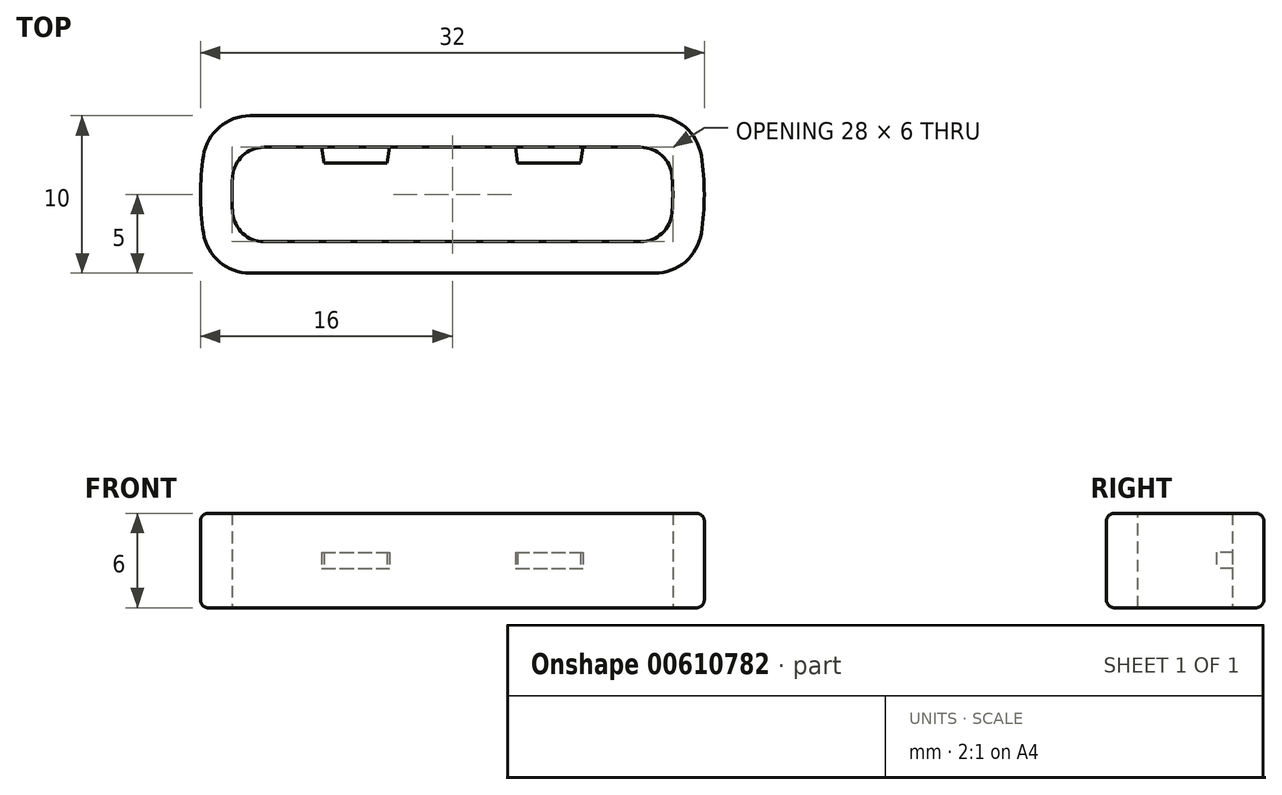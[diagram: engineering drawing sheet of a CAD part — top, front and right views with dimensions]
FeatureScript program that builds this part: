
annotation { "Feature Type Name" : "Feature", "Feature Type Description" : "" }
export const myFeature = defineFeature(function(context is Context, id is Id, definition is map)
    precondition{}
    {
        {
            var Q0;
            Q0=qCreatedBy(makeId("Top.planeOp"),FACE);
            var sketch = newSketch(context, id + "F0", { "sketchPlane" : qUnion([Q0])});
            skArc(sketch, "E0", {"start": v(13.67, -3) * mm, "mid": v(14, 0) * mm, "end": v(13.67, 3) * mm});
            skLineSegment(sketch, "E1.bottom", {"start": v(-13.67, 3) * mm, "end": v(13.67, 3) * mm});
            skLineSegment(sketch, "E1.top", {"start": v(-13.67, -3) * mm, "end": v(13.67, -3) * mm});
            skArc(sketch, "E2", {"start": v(15.2, -5) * mm, "mid": v(16, 0) * mm, "end": v(15.2, 5) * mm});
            skLineSegment(sketch, "E3.bottom", {"start": v(-15.2, 5) * mm, "end": v(15.2, 5) * mm});
            skLineSegment(sketch, "E3.top", {"start": v(-15.2, -5) * mm, "end": v(15.2, -5) * mm});
            skArc(sketch, "E4.trimOffspring", {"start": v(-15.2, 5) * mm, "mid": v(-16, 0) * mm, "end": v(-15.2, -5) * mm});
            skArc(sketch, "E5.trimOffspring", {"start": v(-13.67, 3) * mm, "mid": v(-14, 0) * mm, "end": v(-13.67, -3) * mm});
            skSolve(sketch);
        }
        {
            var Q0;
            Q0=makeQuery(id+"F0.imprint","IMPRINT",FACE,{"disambiguationData":[TD([[makeQuery(id+"F0.imprint","IMPRINT",EDGE,{"derivedFrom":sQuery(id+"F0.wireOp",EDGE,"E0")}),-1.0]])]});
            extrude(context, id + "F1", {"entities" : qUnion([Q0]), "endBound" : BoundingType.SYMMETRIC, "depth" : 6 * mm, "offsetDistance" : 25 * mm});
        }
        {
            var Q0;
            Q0=makeQuery(id+"F1.opExtrude","SWEPT_EDGE",EDGE,{"disambiguationData":[OSD([sQuery(id+"F0.wireOp",EDGE,"E2"),sQuery(id+"F0.wireOp",EDGE,"9OBbbcq9-SRuw-GZlw-vw5F-T3GGpGqtnNip")])]});
            var Q1;
            Q1=makeQuery(id+"F1.opExtrude","SWEPT_EDGE",EDGE,{"disambiguationData":[OSD([sQuery(id+"F0.wireOp",EDGE,"E2"),sQuery(id+"F0.wireOp",EDGE,"KvdtnGYB-6XDc-090E-p4LO-zTu2kdHXZUgR")])]});
            var Q2;
            Q2=makeQuery(id+"F1.opExtrude","SWEPT_EDGE",EDGE,{"disambiguationData":[OSD([sQuery(id+"F0.wireOp",EDGE,"ee8mhABX-Ydh4-nBuw-DtJm-GZrTCmKTSOxF"),sQuery(id+"F0.wireOp",EDGE,"E4.trimOffspring")])]});
            var Q3;
            Q3=makeQuery(id+"F1.opExtrude","SWEPT_EDGE",EDGE,{"disambiguationData":[OSD([sQuery(id+"F0.wireOp",EDGE,"tJgcbcFm-jQ7m-bqbT-wgb3-XuOhf6dTw6rV"),sQuery(id+"F0.wireOp",EDGE,"E4.trimOffspring")])]});
            fillet(context, id + "F2", {"entities" : qUnion([Q0, Q1, Q2, Q3]), "radius" : 3 * mm, "tangentPropagation" : true, "allowEdgeOverflow" : false});
        }
        {
            var Q0;
            Q0=makeQuery(id+"F1.opExtrude","SWEPT_EDGE",EDGE,{"disambiguationData":[OSD([sQuery(id+"F0.wireOp",EDGE,"E0"),sQuery(id+"F0.wireOp",EDGE,"E1.bottom")])]});
            var Q1;
            Q1=makeQuery(id+"F1.opExtrude","SWEPT_EDGE",EDGE,{"disambiguationData":[OSD([sQuery(id+"F0.wireOp",EDGE,"E0"),sQuery(id+"F0.wireOp",EDGE,"E1.top")])]});
            var Q2;
            Q2=makeQuery(id+"F1.opExtrude","SWEPT_EDGE",EDGE,{"disambiguationData":[OSD([sQuery(id+"F0.wireOp",EDGE,"E1.top"),sQuery(id+"F0.wireOp",EDGE,"E5.trimOffspring")])]});
            var Q3;
            Q3=makeQuery(id+"F1.opExtrude","SWEPT_EDGE",EDGE,{"disambiguationData":[OSD([sQuery(id+"F0.wireOp",EDGE,"E1.bottom"),sQuery(id+"F0.wireOp",EDGE,"E5.trimOffspring")])]});
            fillet(context, id + "F3", {"entities" : qUnion([Q0, Q1, Q2, Q3]), "radius" : 2 * mm, "tangentPropagation" : true, "allowEdgeOverflow" : false});
        }
        {
            var Q0;
            Q0=qCreatedBy(makeId("Top.planeOp"),FACE);
            var sketch = newSketch(context, id + "F4", { "sketchPlane" : qUnion([Q0])});
            skLineSegment(sketch, "E6", {"start": v(-8.3, 3) * mm, "end": v(-8.15, 2) * mm});
            skLineSegment(sketch, "E7", {"start": v(-8.15, 2) * mm, "end": v(-4.15, 2) * mm});
            skLineSegment(sketch, "E8", {"start": v(-4.15, 2) * mm, "end": v(-4, 3) * mm});
            skLineSegment(sketch, "E9", {"start": v(-8.3, 3) * mm, "end": v(-4, 3) * mm});
            skLineSegment(sketch, "E10", {"start": v(4, 3) * mm, "end": v(4.15, 2) * mm});
            skLineSegment(sketch, "E11", {"start": v(4.15, 2) * mm, "end": v(8.15, 2) * mm});
            skLineSegment(sketch, "E12", {"start": v(8.15, 2) * mm, "end": v(8.3, 3) * mm});
            skLineSegment(sketch, "E13", {"start": v(4, 3) * mm, "end": v(8.3, 3) * mm});
            skSolve(sketch);
        }
        {
            var Q0;
            Q0 = qSketchRegion(id + "F4", true);
            extrude(context, id + "F5", {"entities" : qUnion([Q0]), "operationType" : NewBodyOperationType.ADD, "endBound" : BoundingType.SYMMETRIC, "depth" : 1 * mm, "offsetDistance" : 25 * mm});
        }
        {
            var Q0;
            Q0=makeQuery(id+"F1.opExtrude","CAP_EDGE",EDGE,{"disambiguationData":[OSD([sQuery(id+"F0.wireOp",EDGE,"E3.top")])],"isStart":false});
            var Q1;
            {var subQ0=sQuery(id+"F0.wireOp",EDGE,"E3.top");var subQ1=sQuery(id+"F0.wireOp",EDGE,"E2");Q1=makeQuery(id+"F2.opFillet","BLEND_EDGE",EDGE,{"blendedFrom":[makeQuery(id+"F1.opExtrude","SWEPT_EDGE",EDGE,{"disambiguationData":[OSD([subQ1,subQ0])]}),makeQuery(id+"F1.opExtrude","CAP_FACE",FACE,{"disambiguationData":[OSD([sQuery(id+"F0.wireOp",EDGE,"E0"),sQuery(id+"F0.wireOp",EDGE,"E1.bottom"),sQuery(id+"F0.wireOp",EDGE,"E1.top"),subQ1,sQuery(id+"F0.wireOp",EDGE,"E3.bottom"),subQ0,sQuery(id+"F0.wireOp",EDGE,"E4.trimOffspring"),sQuery(id+"F0.wireOp",EDGE,"E5.trimOffspring")])],"isStart":false})],"blendedInto":[makeQuery(id+"F1.opExtrude","CAP_FACE",FACE,{"disambiguationData":[OSD([sQuery(id+"F0.wireOp",EDGE,"E0"),sQuery(id+"F0.wireOp",EDGE,"E1.bottom"),sQuery(id+"F0.wireOp",EDGE,"E1.top"),subQ1,sQuery(id+"F0.wireOp",EDGE,"E3.bottom"),subQ0,sQuery(id+"F0.wireOp",EDGE,"E4.trimOffspring"),sQuery(id+"F0.wireOp",EDGE,"E5.trimOffspring")])],"isStart":false})]});}
            var Q2;
            Q2=makeQuery(id+"F1.opExtrude","CAP_EDGE",EDGE,{"disambiguationData":[OSD([sQuery(id+"F0.wireOp",EDGE,"E2")])],"isStart":false});
            var Q3;
            {var subQ0=sQuery(id+"F0.wireOp",EDGE,"E3.bottom");var subQ1=sQuery(id+"F0.wireOp",EDGE,"E2");Q3=makeQuery(id+"F2.opFillet","BLEND_EDGE",EDGE,{"blendedFrom":[makeQuery(id+"F1.opExtrude","SWEPT_EDGE",EDGE,{"disambiguationData":[OSD([subQ1,subQ0])]}),makeQuery(id+"F1.opExtrude","CAP_FACE",FACE,{"disambiguationData":[OSD([sQuery(id+"F0.wireOp",EDGE,"E0"),sQuery(id+"F0.wireOp",EDGE,"E1.bottom"),sQuery(id+"F0.wireOp",EDGE,"E1.top"),subQ1,subQ0,sQuery(id+"F0.wireOp",EDGE,"E3.top"),sQuery(id+"F0.wireOp",EDGE,"E4.trimOffspring"),sQuery(id+"F0.wireOp",EDGE,"E5.trimOffspring")])],"isStart":false})],"blendedInto":[makeQuery(id+"F1.opExtrude","CAP_FACE",FACE,{"disambiguationData":[OSD([sQuery(id+"F0.wireOp",EDGE,"E0"),sQuery(id+"F0.wireOp",EDGE,"E1.bottom"),sQuery(id+"F0.wireOp",EDGE,"E1.top"),subQ1,subQ0,sQuery(id+"F0.wireOp",EDGE,"E3.top"),sQuery(id+"F0.wireOp",EDGE,"E4.trimOffspring"),sQuery(id+"F0.wireOp",EDGE,"E5.trimOffspring")])],"isStart":false})]});}
            var Q4;
            Q4=makeQuery(id+"F1.opExtrude","CAP_EDGE",EDGE,{"disambiguationData":[OSD([sQuery(id+"F0.wireOp",EDGE,"E3.bottom")])],"isStart":false});
            var Q5;
            {var subQ0=sQuery(id+"F0.wireOp",EDGE,"E4.trimOffspring");var subQ1=sQuery(id+"F0.wireOp",EDGE,"E3.top");Q5=makeQuery(id+"F2.opFillet","BLEND_EDGE",EDGE,{"blendedFrom":[makeQuery(id+"F1.opExtrude","SWEPT_EDGE",EDGE,{"disambiguationData":[OSD([subQ1,subQ0])]}),makeQuery(id+"F1.opExtrude","CAP_FACE",FACE,{"disambiguationData":[OSD([sQuery(id+"F0.wireOp",EDGE,"E0"),sQuery(id+"F0.wireOp",EDGE,"E1.bottom"),sQuery(id+"F0.wireOp",EDGE,"E1.top"),sQuery(id+"F0.wireOp",EDGE,"E2"),sQuery(id+"F0.wireOp",EDGE,"E3.bottom"),subQ1,subQ0,sQuery(id+"F0.wireOp",EDGE,"E5.trimOffspring")])],"isStart":false})],"blendedInto":[makeQuery(id+"F1.opExtrude","CAP_FACE",FACE,{"disambiguationData":[OSD([sQuery(id+"F0.wireOp",EDGE,"E0"),sQuery(id+"F0.wireOp",EDGE,"E1.bottom"),sQuery(id+"F0.wireOp",EDGE,"E1.top"),sQuery(id+"F0.wireOp",EDGE,"E2"),sQuery(id+"F0.wireOp",EDGE,"E3.bottom"),subQ1,subQ0,sQuery(id+"F0.wireOp",EDGE,"E5.trimOffspring")])],"isStart":false})]});}
            var Q6;
            Q6=makeQuery(id+"F1.opExtrude","CAP_EDGE",EDGE,{"disambiguationData":[OSD([sQuery(id+"F0.wireOp",EDGE,"E4.trimOffspring")])],"isStart":false});
            var Q7;
            {var subQ0=sQuery(id+"F0.wireOp",EDGE,"E4.trimOffspring");var subQ1=sQuery(id+"F0.wireOp",EDGE,"E3.bottom");Q7=makeQuery(id+"F2.opFillet","BLEND_EDGE",EDGE,{"blendedFrom":[makeQuery(id+"F1.opExtrude","SWEPT_EDGE",EDGE,{"disambiguationData":[OSD([subQ1,subQ0])]}),makeQuery(id+"F1.opExtrude","CAP_FACE",FACE,{"disambiguationData":[OSD([sQuery(id+"F0.wireOp",EDGE,"E0"),sQuery(id+"F0.wireOp",EDGE,"E1.bottom"),sQuery(id+"F0.wireOp",EDGE,"E1.top"),sQuery(id+"F0.wireOp",EDGE,"E2"),subQ1,sQuery(id+"F0.wireOp",EDGE,"E3.top"),subQ0,sQuery(id+"F0.wireOp",EDGE,"E5.trimOffspring")])],"isStart":false})],"blendedInto":[makeQuery(id+"F1.opExtrude","CAP_FACE",FACE,{"disambiguationData":[OSD([sQuery(id+"F0.wireOp",EDGE,"E0"),sQuery(id+"F0.wireOp",EDGE,"E1.bottom"),sQuery(id+"F0.wireOp",EDGE,"E1.top"),sQuery(id+"F0.wireOp",EDGE,"E2"),subQ1,sQuery(id+"F0.wireOp",EDGE,"E3.top"),subQ0,sQuery(id+"F0.wireOp",EDGE,"E5.trimOffspring")])],"isStart":false})]});}
            var Q8;
            Q8=makeQuery(id+"F1.opExtrude","CAP_EDGE",EDGE,{"disambiguationData":[OSD([sQuery(id+"F0.wireOp",EDGE,"E4.trimOffspring")])],"isStart":true});
            var Q9;
            {var subQ0=sQuery(id+"F0.wireOp",EDGE,"E4.trimOffspring");var subQ1=sQuery(id+"F0.wireOp",EDGE,"E3.bottom");Q9=makeQuery(id+"F2.opFillet","BLEND_EDGE",EDGE,{"blendedFrom":[makeQuery(id+"F1.opExtrude","SWEPT_EDGE",EDGE,{"disambiguationData":[OSD([subQ1,subQ0])]}),makeQuery(id+"F1.opExtrude","CAP_FACE",FACE,{"disambiguationData":[OSD([sQuery(id+"F0.wireOp",EDGE,"E0"),sQuery(id+"F0.wireOp",EDGE,"E1.bottom"),sQuery(id+"F0.wireOp",EDGE,"E1.top"),sQuery(id+"F0.wireOp",EDGE,"E2"),subQ1,sQuery(id+"F0.wireOp",EDGE,"E3.top"),subQ0,sQuery(id+"F0.wireOp",EDGE,"E5.trimOffspring")])],"isStart":true})],"blendedInto":[makeQuery(id+"F1.opExtrude","CAP_FACE",FACE,{"disambiguationData":[OSD([sQuery(id+"F0.wireOp",EDGE,"E0"),sQuery(id+"F0.wireOp",EDGE,"E1.bottom"),sQuery(id+"F0.wireOp",EDGE,"E1.top"),sQuery(id+"F0.wireOp",EDGE,"E2"),subQ1,sQuery(id+"F0.wireOp",EDGE,"E3.top"),subQ0,sQuery(id+"F0.wireOp",EDGE,"E5.trimOffspring")])],"isStart":true})]});}
            var Q10;
            {var subQ0=sQuery(id+"F0.wireOp",EDGE,"E4.trimOffspring");var subQ1=sQuery(id+"F0.wireOp",EDGE,"E3.top");Q10=makeQuery(id+"F2.opFillet","BLEND_EDGE",EDGE,{"blendedFrom":[makeQuery(id+"F1.opExtrude","SWEPT_EDGE",EDGE,{"disambiguationData":[OSD([subQ1,subQ0])]}),makeQuery(id+"F1.opExtrude","CAP_FACE",FACE,{"disambiguationData":[OSD([sQuery(id+"F0.wireOp",EDGE,"E0"),sQuery(id+"F0.wireOp",EDGE,"E1.bottom"),sQuery(id+"F0.wireOp",EDGE,"E1.top"),sQuery(id+"F0.wireOp",EDGE,"E2"),sQuery(id+"F0.wireOp",EDGE,"E3.bottom"),subQ1,subQ0,sQuery(id+"F0.wireOp",EDGE,"E5.trimOffspring")])],"isStart":true})],"blendedInto":[makeQuery(id+"F1.opExtrude","CAP_FACE",FACE,{"disambiguationData":[OSD([sQuery(id+"F0.wireOp",EDGE,"E0"),sQuery(id+"F0.wireOp",EDGE,"E1.bottom"),sQuery(id+"F0.wireOp",EDGE,"E1.top"),sQuery(id+"F0.wireOp",EDGE,"E2"),sQuery(id+"F0.wireOp",EDGE,"E3.bottom"),subQ1,subQ0,sQuery(id+"F0.wireOp",EDGE,"E5.trimOffspring")])],"isStart":true})]});}
            var Q11;
            Q11=makeQuery(id+"F1.opExtrude","CAP_EDGE",EDGE,{"disambiguationData":[OSD([sQuery(id+"F0.wireOp",EDGE,"E3.top")])],"isStart":true});
            var Q12;
            Q12=makeQuery(id+"F1.opExtrude","CAP_EDGE",EDGE,{"disambiguationData":[OSD([sQuery(id+"F0.wireOp",EDGE,"E3.bottom")])],"isStart":true});
            var Q13;
            {var subQ0=sQuery(id+"F0.wireOp",EDGE,"E3.top");var subQ1=sQuery(id+"F0.wireOp",EDGE,"E2");Q13=makeQuery(id+"F2.opFillet","BLEND_EDGE",EDGE,{"blendedFrom":[makeQuery(id+"F1.opExtrude","SWEPT_EDGE",EDGE,{"disambiguationData":[OSD([subQ1,subQ0])]}),makeQuery(id+"F1.opExtrude","CAP_FACE",FACE,{"disambiguationData":[OSD([sQuery(id+"F0.wireOp",EDGE,"E0"),sQuery(id+"F0.wireOp",EDGE,"E1.bottom"),sQuery(id+"F0.wireOp",EDGE,"E1.top"),subQ1,sQuery(id+"F0.wireOp",EDGE,"E3.bottom"),subQ0,sQuery(id+"F0.wireOp",EDGE,"E4.trimOffspring"),sQuery(id+"F0.wireOp",EDGE,"E5.trimOffspring")])],"isStart":true})],"blendedInto":[makeQuery(id+"F1.opExtrude","CAP_FACE",FACE,{"disambiguationData":[OSD([sQuery(id+"F0.wireOp",EDGE,"E0"),sQuery(id+"F0.wireOp",EDGE,"E1.bottom"),sQuery(id+"F0.wireOp",EDGE,"E1.top"),subQ1,sQuery(id+"F0.wireOp",EDGE,"E3.bottom"),subQ0,sQuery(id+"F0.wireOp",EDGE,"E4.trimOffspring"),sQuery(id+"F0.wireOp",EDGE,"E5.trimOffspring")])],"isStart":true})]});}
            var Q14;
            Q14=makeQuery(id+"F1.opExtrude","CAP_EDGE",EDGE,{"disambiguationData":[OSD([sQuery(id+"F0.wireOp",EDGE,"E2")])],"isStart":true});
            var Q15;
            {var subQ0=sQuery(id+"F0.wireOp",EDGE,"E3.bottom");var subQ1=sQuery(id+"F0.wireOp",EDGE,"E2");Q15=makeQuery(id+"F2.opFillet","BLEND_EDGE",EDGE,{"blendedFrom":[makeQuery(id+"F1.opExtrude","SWEPT_EDGE",EDGE,{"disambiguationData":[OSD([subQ1,subQ0])]}),makeQuery(id+"F1.opExtrude","CAP_FACE",FACE,{"disambiguationData":[OSD([sQuery(id+"F0.wireOp",EDGE,"E0"),sQuery(id+"F0.wireOp",EDGE,"E1.bottom"),sQuery(id+"F0.wireOp",EDGE,"E1.top"),subQ1,subQ0,sQuery(id+"F0.wireOp",EDGE,"E3.top"),sQuery(id+"F0.wireOp",EDGE,"E4.trimOffspring"),sQuery(id+"F0.wireOp",EDGE,"E5.trimOffspring")])],"isStart":true})],"blendedInto":[makeQuery(id+"F1.opExtrude","CAP_FACE",FACE,{"disambiguationData":[OSD([sQuery(id+"F0.wireOp",EDGE,"E0"),sQuery(id+"F0.wireOp",EDGE,"E1.bottom"),sQuery(id+"F0.wireOp",EDGE,"E1.top"),subQ1,subQ0,sQuery(id+"F0.wireOp",EDGE,"E3.top"),sQuery(id+"F0.wireOp",EDGE,"E4.trimOffspring"),sQuery(id+"F0.wireOp",EDGE,"E5.trimOffspring")])],"isStart":true})]});}
            fillet(context, id + "F6", {"entities" : qUnion([Q0, Q1, Q2, Q3, Q4, Q5, Q6, Q7, Q8, Q9, Q10, Q11, Q12, Q13, Q14, Q15]), "radius" : 0.5 * mm, "tangentPropagation" : true, "allowEdgeOverflow" : false});
        }
    });
